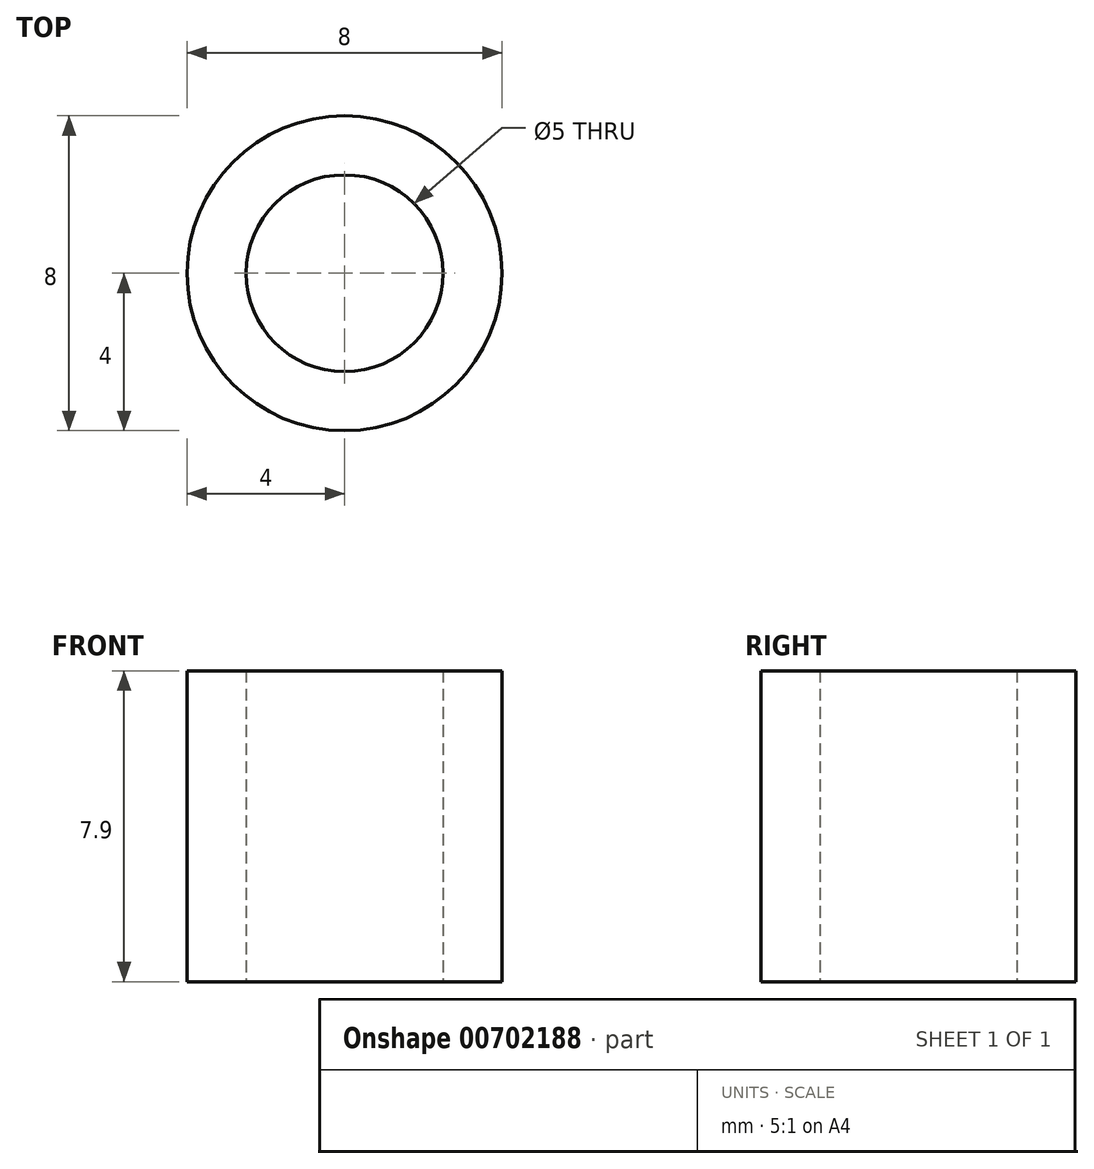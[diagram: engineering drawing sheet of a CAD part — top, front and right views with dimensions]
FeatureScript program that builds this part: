
annotation { "Feature Type Name" : "Feature", "Feature Type Description" : "" }
export const myFeature = defineFeature(function(context is Context, id is Id, definition is map)
    precondition{}
    {
        {
            var Q0;
            Q0=qCreatedBy(makeId("Top.planeOp"),FACE);
            var sketch = newSketch(context, id + "F0", { "sketchPlane" : qUnion([Q0])});
            skCircle(sketch, "E0", {"center": v(0, 0) * mm, "radius": 4 * mm});
            skCircle(sketch, "E1", {"center": v(0, 0) * mm, "radius": 2.5 * mm});
            skSolve(sketch);
        }
        {
            var Q0;
            Q0 = qSketchRegion(id + "F0", true);
            extrude(context, id + "F1", {"entities" : qUnion([Q0]), "depth" : 7.9 * mm, "offsetDistance" : 25 * mm});
        }
    });
